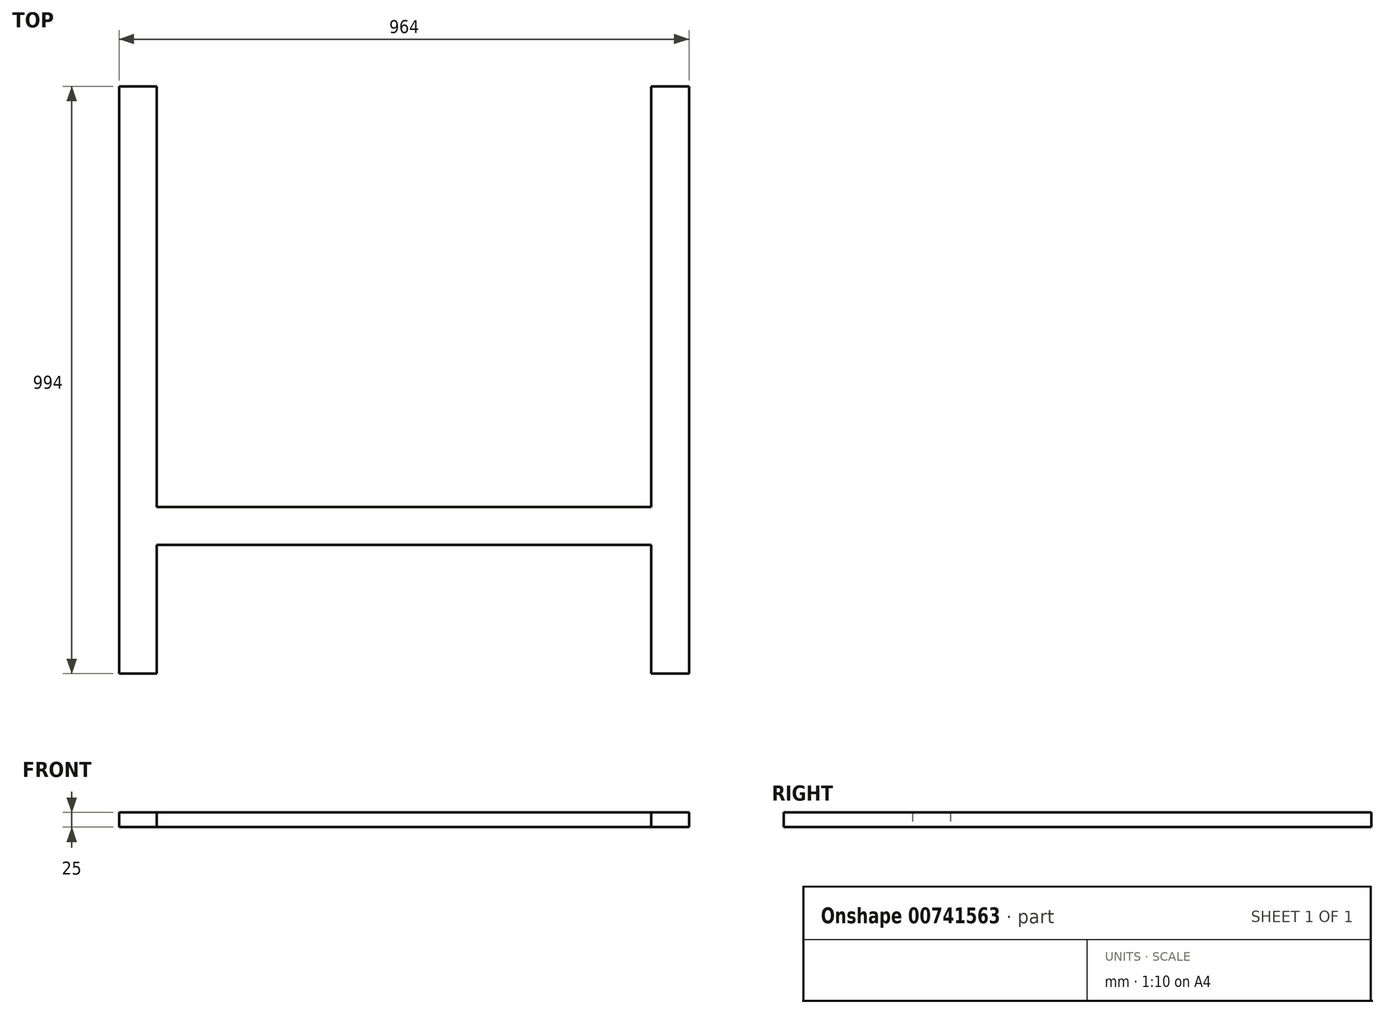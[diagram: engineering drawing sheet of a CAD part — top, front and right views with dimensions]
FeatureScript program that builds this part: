
annotation { "Feature Type Name" : "Feature", "Feature Type Description" : "" }
export const myFeature = defineFeature(function(context is Context, id is Id, definition is map)
    precondition{}
    {
        {
            var Q0;
            Q0=qCreatedBy(makeId("Top.planeOp"),FACE);
            var sketch = newSketch(context, id + "F0", { "sketchPlane" : qUnion([Q0])});
            skLineSegment(sketch, "E0.bottom", {"start": v(-418, 32) * mm, "end": v(418, 32) * mm});
            skLineSegment(sketch, "E0.top", {"start": v(-418, -32) * mm, "end": v(418, -32) * mm});
            skPoint(sketch, "E0.middle", {"position": v(0, 0) * mm});
            skLineSegment(sketch, "E1", {"start": v(-418, 32) * mm, "end": v(-418, 744) * mm});
            skLineSegment(sketch, "E2", {"start": v(-418, 744) * mm, "end": v(-482, 744) * mm});
            skLineSegment(sketch, "E3", {"start": v(-482, 744) * mm, "end": v(-482, -250) * mm});
            skLineSegment(sketch, "E4", {"start": v(-482, -250) * mm, "end": v(-418, -250) * mm});
            skLineSegment(sketch, "E5", {"start": v(-418, -250) * mm, "end": v(-418, -32) * mm});
            skLineSegment(sketch, "E6", {"start": v(418, 32) * mm, "end": v(418, 744) * mm});
            skLineSegment(sketch, "E7", {"start": v(418, 744) * mm, "end": v(482, 744) * mm});
            skLineSegment(sketch, "E8", {"start": v(482, 744) * mm, "end": v(482, -250) * mm});
            skLineSegment(sketch, "E9", {"start": v(482, -250) * mm, "end": v(418, -250) * mm});
            skLineSegment(sketch, "E10", {"start": v(418, -250) * mm, "end": v(418, -32) * mm});
            skSolve(sketch);
        }
        {
            var Q0;
            Q0=qSketchRegion(id+"F0",true);
            extrude(context, id + "F1", {"entities" : qUnion([Q0]), "depth" : 25 * mm, "offsetDistance" : 25 * mm});
        }
    });
